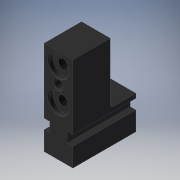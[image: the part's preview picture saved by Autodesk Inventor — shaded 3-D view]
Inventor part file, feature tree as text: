
AUTODESK INVENTOR PART (.ipt)
format: ipt  version: 2019 (Build 230136000, 136)  size: 179,712 bytes
history: native  units: mm
features: other x21, sketch x6, extrude x3, revolve x3, thread x2
ambient origin geometry x8: Origin, YZ Plane, XZ Plane, XY Plane, X Axis, Y Axis, Z Axis, Center Point
bodies: Solid1 (feature_tree)
feature tree (35):
  extrude  "Extrusion1"  Depth=10.0mm TaperAngle=0.0deg
  extrude  "Extrusion2"  TaperAngle=360.0deg  [1 undecoded]
  revolve  "Revolution1"  Angle=360.0deg
  revolve  "Revolution2"  [1 undecoded]
  thread  "Thread1"  [1 undecoded]
  revolve  "Revolution3"  [1 undecoded]
  thread  "Thread2"  [1 undecoded]
  extrude  "Extrusion3"  [1 undecoded]
  other  "GRIFF_XY"
  other  "GRIFF_YZ"
  other  "GRIFF_ZX"
  other  "GRIFF_X"
  other  "GRIFF_Y"
  other  "GRIFF_Z"
  other  "GRIFF_Center"
  other  "TO_ZBH_1_XY"
  other  "TO_ZBH_1_YZ"
  other  "TO_ZBH_1_ZX"
  other  "TO_ZBH_1_X"
  other  "TO_ZBH_1_Y"
  other  "TO_ZBH_1_Z"
  other  "TO_ZBH_1_Center"
  other  "TO_ZBH_2_XY"
  other  "TO_ZBH_2_YZ"
  other  "TO_ZBH_2_ZX"
  other  "TO_ZBH_2_X"
  other  "TO_ZBH_2_Y"
  other  "TO_ZBH_2_Z"
  other  "TO_ZBH_2_Center"
  sketch  "Sketch_1"  dims[d0=21.9mm d1=0.0mm d2=10.0mm d3=0.0mm]
  sketch  "Sketch_2"  dims[d4=360.0deg d5=360.0deg]
  sketch  "Sketch_5"  dims[d6=11.4mm d7=0.0mm d8=360.0deg]
  sketch  "Sketch_6"  dims[d9=11.4mm d10=0.0mm d11=1.5mm d12=0.0mm d13=0.0mm d14=0.0mm d15=0.0mm]
  sketch  "Sketch_7"
  sketch  "Sketch_10"
note: 6 required parameter values undecoded (feature->parameter linkage not recoverable at this tier; creation-order binding heuristic only, values carry confidence <= 0.55)